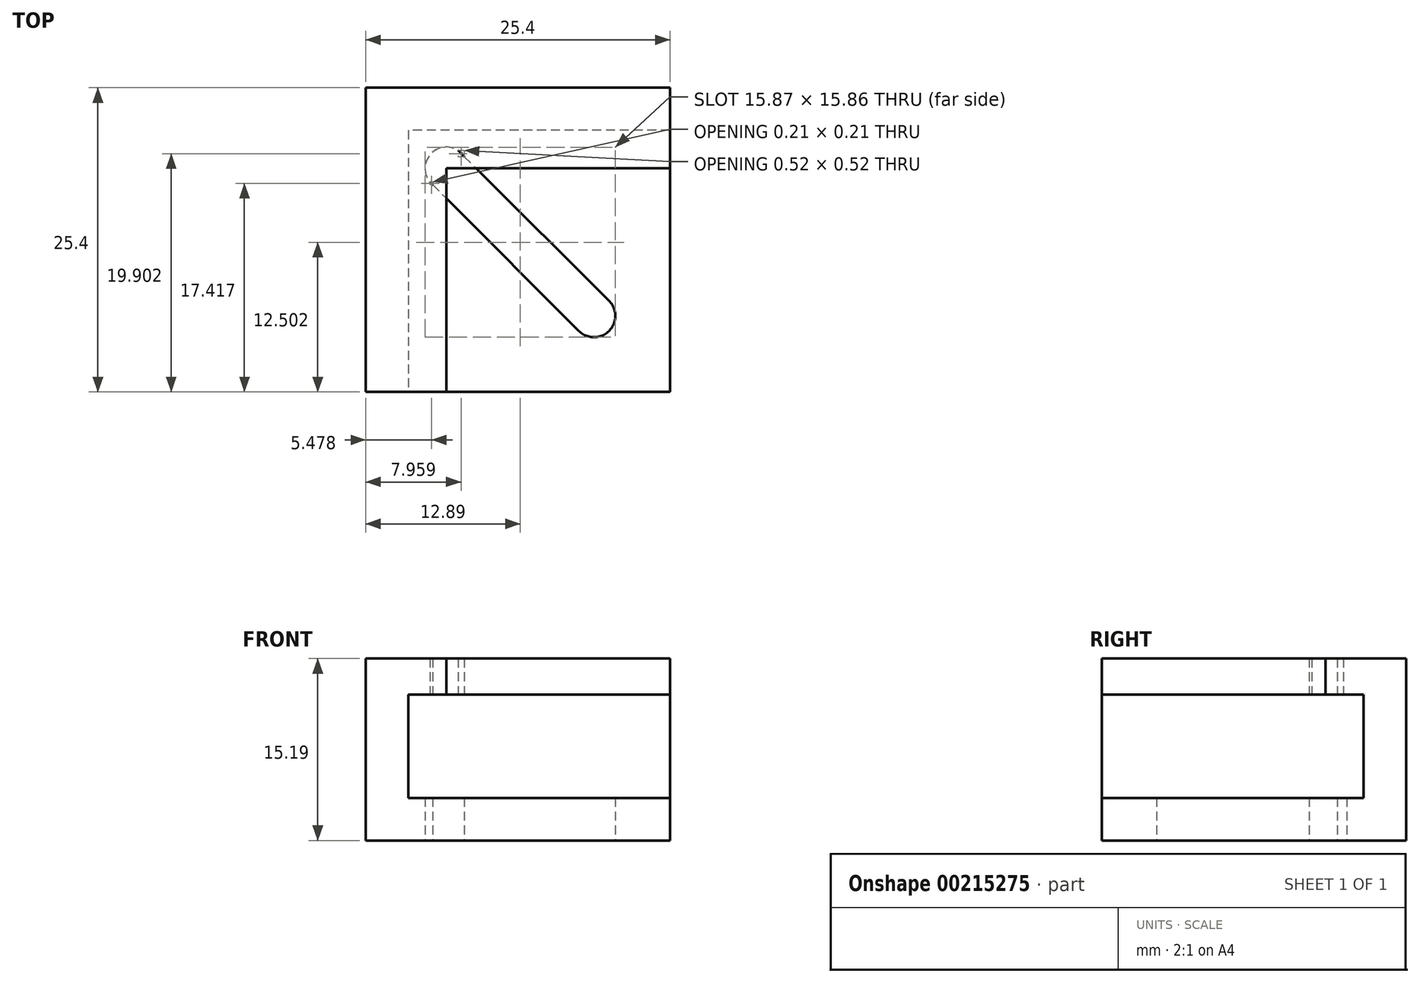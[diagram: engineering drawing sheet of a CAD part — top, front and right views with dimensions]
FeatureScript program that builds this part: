
annotation { "Feature Type Name" : "Feature", "Feature Type Description" : "" }
export const myFeature = defineFeature(function(context is Context, id is Id, definition is map)
    precondition{}
    {
        {
            var Q0;
            Q0=qCreatedBy(makeId("Top.planeOp"),FACE);
            var sketch = newSketch(context, id + "F0", { "sketchPlane" : qUnion([Q0])});
            skLineSegment(sketch, "E0.bottom", {"start": v(0, 0) * mm, "end": v(25.4, 0) * mm});
            skLineSegment(sketch, "E0.top", {"start": v(0, 25.4) * mm, "end": v(25.4, 25.4) * mm});
            skLineSegment(sketch, "E0.left", {"start": v(0, 0) * mm, "end": v(0, 25.4) * mm});
            skLineSegment(sketch, "E0.right", {"start": v(25.4, 0) * mm, "end": v(25.4, 25.4) * mm});
            skLineSegment(sketch, "E1", {"start": v(0, 0) * mm, "end": v(3.56, 0) * mm});
            skLineSegment(sketch, "E2", {"start": v(3.56, 0) * mm, "end": v(3.56, 21.84) * mm});
            skLineSegment(sketch, "E3", {"start": v(3.56, 21.84) * mm, "end": v(25.4, 21.84) * mm});
            skLineSegment(sketch, "E4", {"start": v(25.4, 21.84) * mm, "end": v(25.4, 25.4) * mm});
            skLineSegment(sketch, "E5", {"start": v(3.56, 0) * mm, "end": v(6.73, 0) * mm});
            skLineSegment(sketch, "E6", {"start": v(25.4, 21.84) * mm, "end": v(25.4, 18.67) * mm});
            skLineSegment(sketch, "E7", {"start": v(25.4, 18.67) * mm, "end": v(6.73, 18.67) * mm});
            skLineSegment(sketch, "E8", {"start": v(6.73, 18.67) * mm, "end": v(6.73, 0) * mm});
            skCircle(sketch, "E9", {"center": v(6.73, 18.67) * mm, "radius": 1.78 * mm});
            skLineSegment(sketch, "E10", {"start": v(25.4, 0) * mm, "end": v(19.05, 0) * mm});
            skLineSegment(sketch, "E11", {"start": v(19.05, 0) * mm, "end": v(19.05, 6.35) * mm});
            skCircle(sketch, "E12", {"center": v(19.05, 6.35) * mm, "radius": 1.78 * mm});
            skLineSegment(sketch, "E13", {"start": v(7.7, 20.16) * mm, "end": v(20.3, 7.6) * mm});
            skLineSegment(sketch, "E14", {"start": v(5.37, 17.52) * mm, "end": v(17.8, 5.1) * mm});
            skSolve(sketch);
        }
        {
            var Q0;
            Q0 = qSketchRegion(id + "F0", true);
            extrude(context, id + "F1", {"entities" : qUnion([Q0]), "depth" : 3.56 * mm});
        }
        {
            var Q0;
            Q0=makeQuery(id+"F0.imprint","IMPRINT",FACE,{"disambiguationData":[TD([[makeQuery(id+"F0.imprint","IMPRINT",EDGE,{"derivedFrom":sQuery(id+"F0.wireOp",EDGE,"E0.top")}),-1.0]])]});
            extrude(context, id + "F2", {"entities" : qUnion([Q0]), "operationType" : NewBodyOperationType.ADD, "depth" : 12.2 * mm});
        }
        {
            var Q0;
            Q0=makeQuery(id+"F0.imprint","IMPRINT",FACE,{"disambiguationData":[TD([[makeQuery(id+"F0.imprint","IMPRINT",EDGE,{"derivedFrom":sQuery(id+"F0.wireOp",EDGE,"E2")}),-1.0]])]});
            var Q1;
            {var subQ5=sQuery(id+"F0.wireOp",EDGE,"E7");var subQ8=sQuery(id+"F0.wireOp",EDGE,"E8");var subQ9=makeQuery(id+"F0.imprint","INTERSECT",VERTEX,{"derivedFrom":[subQ5,subQ8]});Q1=makeQuery(id+"F0.imprint","IMPRINT",FACE,{"disambiguationData":[TD([[makeQuery(id+"F0.imprint","IMPRINT",EDGE,{"disambiguationData":[TD([[subQ9,1.0]])],"derivedFrom":subQ5}),-1.0]])]});}
            var Q2;
            {var subQ0=sQuery(id+"F0.wireOp",EDGE,"E9");var subQ1=sQuery(id+"F0.wireOp",EDGE,"E8");var subQ2=makeQuery(id+"F0.imprint","INTERSECT",VERTEX,{"derivedFrom":[subQ1,subQ0]});Q2=makeQuery(id+"F0.imprint","IMPRINT",FACE,{"disambiguationData":[TD([[makeQuery(id+"F0.imprint","IMPRINT",EDGE,{"disambiguationData":[TD([[subQ2,-1.0]])],"derivedFrom":subQ1}),-1.0]])]});}
            var Q3;
            {var subQ0=sQuery(id+"F0.wireOp",EDGE,"E13");var subQ1=sQuery(id+"F0.wireOp",EDGE,"E7");var subQ2=makeQuery(id+"F0.imprint","INTERSECT",VERTEX,{"derivedFrom":[subQ1,subQ0]});Q3=makeQuery(id+"F0.imprint","IMPRINT",FACE,{"disambiguationData":[TD([[makeQuery(id+"F0.imprint","IMPRINT",EDGE,{"disambiguationData":[TD([[subQ2,-1.0]])],"derivedFrom":subQ1}),-1.0]])]});}
            var Q4;
            Q4=makeQuery(id+"F0.imprint","IMPRINT",FACE,{"disambiguationData":[TD([[makeQuery(id+"F0.imprint","IMPRINT",EDGE,{"derivedFrom":sQuery(id+"F0.wireOp",EDGE,"E0.top")}),-1.0]])]});
            extrude(context, id + "F3", {"entities" : qUnion([Q0, Q1, Q2, Q3, Q4]), "operationType" : NewBodyOperationType.ADD, "depth" : 15.2 * mm, "hasSecondDirection" : true, "secondDirectionOppositeDirection" : false, "secondDirectionDepth" : 12.2 * mm});
        }
    });
